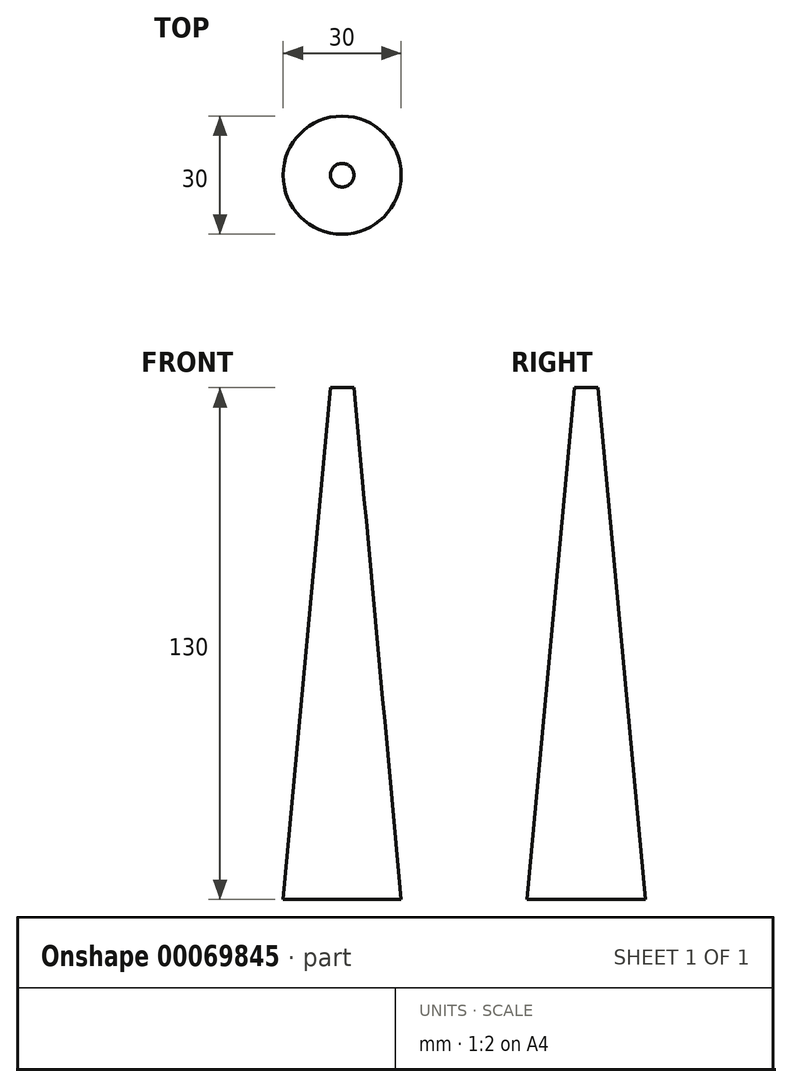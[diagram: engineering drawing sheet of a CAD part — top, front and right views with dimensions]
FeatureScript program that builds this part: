
annotation { "Feature Type Name" : "Feature", "Feature Type Description" : "" }
export const myFeature = defineFeature(function(context is Context, id is Id, definition is map)
    precondition{}
    {
        {
            var Q0;
            Q0=qCreatedBy(makeId("Top.planeOp"),FACE);
            var sketch = newSketch(context, id + "F0", { "sketchPlane" : qUnion([Q0])});
            skCircle(sketch, "E0", {"center": v(0, 0) * mm, "radius": 15 * mm});
            skSolve(sketch);
        }
        {
            var Q0;
            Q0 = qSketchRegion(id + "F0", true);
            extrude(context, id + "F1", {"entities" : qUnion([Q0]), "depth" : 130 * mm});
        }
        {
            var Q0;
            Q0=makeQuery(id+"F1.opExtrude","CAP_EDGE",EDGE,{"disambiguationData":[OSD([sQuery(id+"F0.wireOp",EDGE,"E0")])],"isStart":false});
            chamfer(context, id + "F2", {"entities" : qUnion([Q0]), "chamferType" : ChamferType.TWO_OFFSETS, "width1" : 12 * mm, "oppositeDirection" : false, "width2" : 130 * mm, "tangentPropagation" : true});
        }
    });
